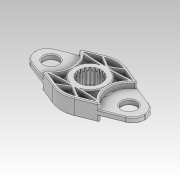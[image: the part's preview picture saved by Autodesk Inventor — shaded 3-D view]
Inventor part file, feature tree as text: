
AUTODESK INVENTOR PART (.ipt)
format: ipt  version: 2020 (Build 240168000, 168)  size: 1,318,912 bytes
history: native  units: mm
features: sketch x10, extrude x8, other x7, fillet x4, revolve x3, pattern_circular x1, imported_body x1, projected_geometry x1
ambient origin geometry x8: Origin, YZ Plane, XZ Plane, XY Plane, X Axis, Y Axis, Z Axis, Center Point
bodies: Solid1 (feature_tree)
feature tree (35):
  other  "HD_mastersketch.ipt"
  other  "Blocks"
  revolve  "Revolution1"  [1 undecoded]
  extrude  "Extrusion1"  Depth=5.0mm
  extrude  "Extrusion2"  TaperAngle=0.0deg  [1 undecoded]
  fillet  "Fillet1"  [1 undecoded]
  extrude  "Extrusion7"  Depth=12.6mm
  extrude  "Extrusion10"  TaperAngle=0.0deg  [1 undecoded]
  pattern_circular  "Circular Pattern1"  [2 undecoded]
  revolve  "Revolution3"  [1 undecoded]
  extrude  "Extrusion12"  Depth=1.0mm TaperAngle=0.0deg
  fillet  "Fillet7"  Radius=200.0mm
  fillet  "Fillet5"  Radius=0.2mm
  fillet  "Fillet6"  [1 undecoded]
  revolve  "Revolution4"  [1 undecoded]
  extrude  "Extrusion13"  Depth=1.0mm
  extrude  "Extrusion8"  Depth=1.0mm
  extrude  "Extrusion9"  Depth=1.0mm
  other  "608 bearing"
  other  "Belt"
  other  "Rotor"
  imported_body  "Base"
  sketch  "Sketch8"  dims[d1=10.0mm d24=7.0mm d25=22.0mm d26=8.0mm]
  sketch  "Sketch9"  dims[d2=90.0deg d3=5.0mm d4=10.0mm]
  sketch  "Sketch15"  dims[d5=15.0mm d6=0.0mm d7=0.0mm d8=0.0mm d9=0.0mm]
  sketch  "Sketch16"  dims[d10=7.0mm d44=12.6mm]
  sketch  "Sketch17"  dims[d45=10.0mm d46=0.0mm d47=0.0mm d48=0.0mm]
  sketch  "Sketch18"  dims[d49=4.5mm d50=0.0mm]
  sketch  "Sketch19"  dims[d51=8.726646mm]
  sketch  "Sketch20"  dims[d52=1.0mm]
  sketch  "Sketch22"  dims[d53=90.0deg]
  projected_geometry  "Projected Loop2"
  sketch  "Sketch23"  dims[d54=0.5mm d55=0.75mm d56=10.9mm d58=4.5mm d59=0.0mm d60=200.0mm d61=360.0deg d63=0.2mm d78=90.0deg d82=12.6mm d84=24.0mm d88=1.5mm d89=23.0mm d90=1.5mm d91=10.0mm d92=0.0mm d93=1.0mm d94=1.0mm d95=4.1mm d96=6.0mm d97=2.0mm d98=45.0deg d99=0.8mm d100=2.0mm d101=0.5mm d102=0.5mm d103=1.0mm d104=10.0mm d105=0.0mm]
  other  "608 bearing:1"
  other  "608 bearing:2"
note: 9 required parameter values undecoded (feature->parameter linkage not recoverable at this tier; creation-order binding heuristic only, values carry confidence <= 0.55)